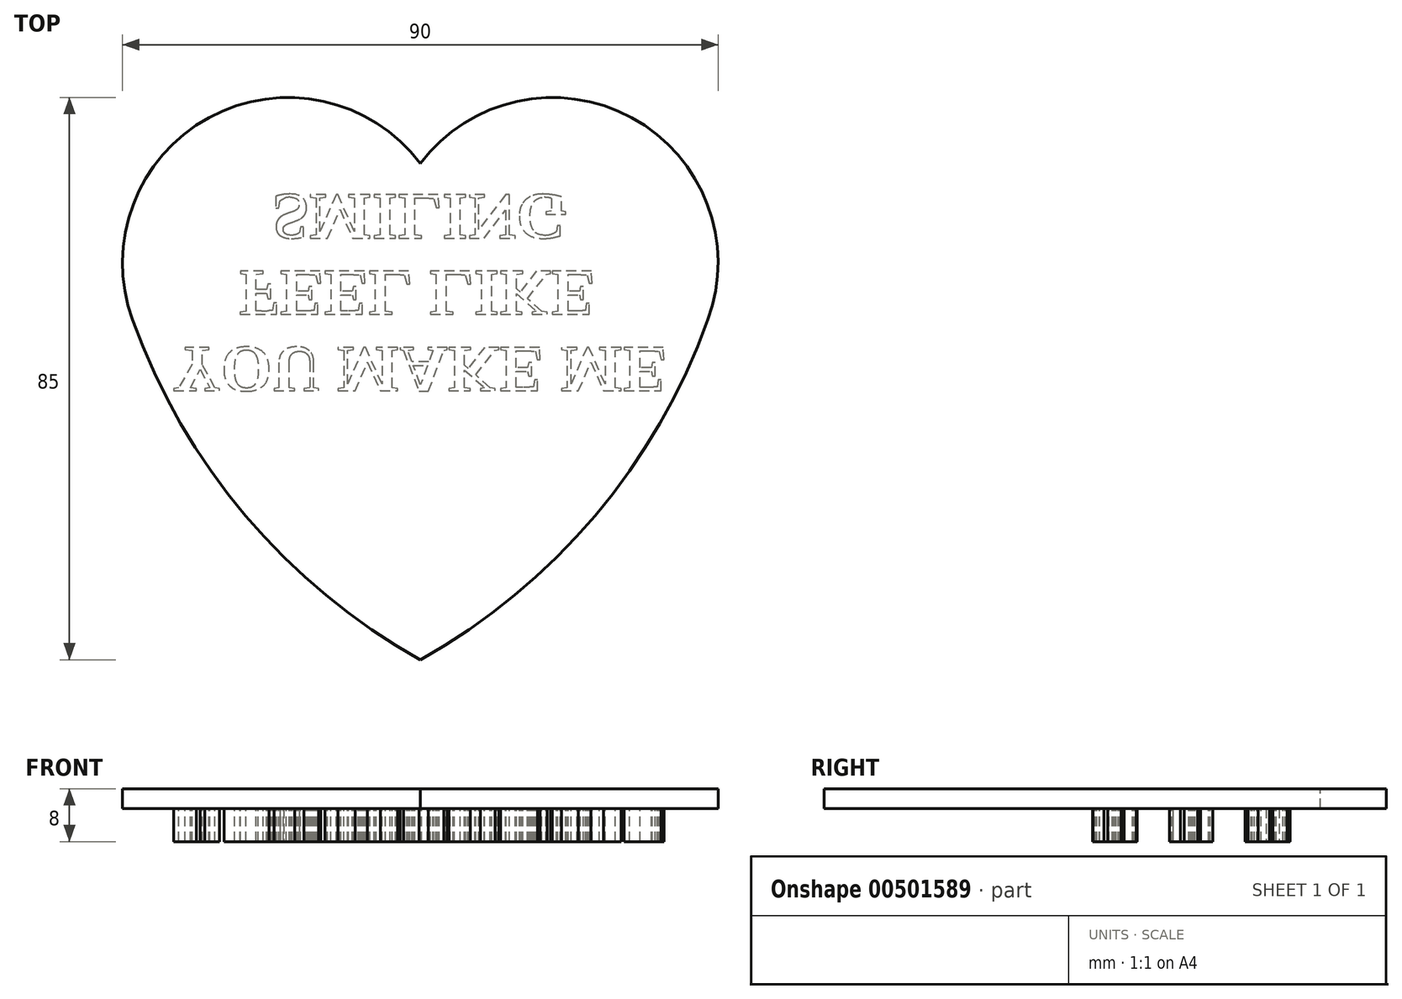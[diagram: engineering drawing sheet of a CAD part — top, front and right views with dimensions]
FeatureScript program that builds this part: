
annotation { "Feature Type Name" : "Feature", "Feature Type Description" : "" }
export const myFeature = defineFeature(function(context is Context, id is Id, definition is map)
    precondition{}
    {
        {
            var Q0;
            Q0=qCreatedBy(makeId("Top.planeOp"),FACE);
            var sketch = newSketch(context, id + "F0", { "sketchPlane" : qUnion([Q0])});
            skArc(sketch, "E0", {"start": v(-43.47, 1.39) * mm, "mid": v(-26.4, -28.25) * mm, "end": v(0, -50) * mm});
            skArc(sketch, "E1", {"start": v(0, 25) * mm, "mid": v(-31.93, 31.97) * mm, "end": v(-43.47, 1.39) * mm});
            skArc(sketch, "E2.MirrorCS", {"start": v(0, 25) * mm, "mid": v(31.93, 31.97) * mm, "end": v(43.47, 1.39) * mm});
            skArc(sketch, "E3.MirrorCS", {"start": v(43.47, 1.39) * mm, "mid": v(26.4, -28.25) * mm, "end": v(0, -50) * mm});
            skSolve(sketch);
        }
        {
            var Q0;
            Q0=qSketchRegion(id+"F0",true);
            extrude(context, id + "F1", {"entities" : qUnion([Q0]), "oppositeDirection" : true, "depth" : 3 * mm});
        }
        {
            var Q0;
            Q0=makeQuery(id+"F1.opExtrude","CAP_FACE",FACE,{"disambiguationData":[OSD([sQuery(id+"F0.wireOp",EDGE,"E0"),sQuery(id+"F0.wireOp",EDGE,"E1"),sQuery(id+"F0.wireOp",EDGE,"E2.MirrorCS"),sQuery(id+"F0.wireOp",EDGE,"E3.MirrorCS")])],"isStart":false});
            var sketch = newSketch(context, id + "F2", { "sketchPlane" : qUnion([Q0])});
            skText(sketch, "E4", { "text": "YOU MAKE ME   \n    FEEL LIKE \n      SMILING", "fontName": "Tinos-Bold.ttf"});
            const initialGuessF2  = {"E4": [-0.03742, 0.00277, 1, 0, 0.00723]};
            skSetInitialGuess(sketch, initialGuessF2);
            skSolve(sketch);
        }
        {
            var Q0;
            Q0=qSketchRegion(id+"F2",true);
            extrude(context, id + "F3", {"entities" : qUnion([Q0]), "operationType" : NewBodyOperationType.ADD, "depth" : 5 * mm});
        }
    });
